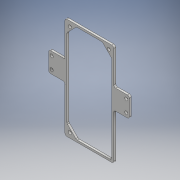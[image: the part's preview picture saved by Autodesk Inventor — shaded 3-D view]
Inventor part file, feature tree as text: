
AUTODESK INVENTOR PART (.ipt)
format: ipt  version: 2017 (Build 210142000, 142)  size: 189,952 bytes
history: native  units: mm
features: extrude x1, fillet x1, sketch x1
ambient origin geometry x8: Origin, YZ Plane, XZ Plane, XY Plane, X Axis, Y Axis, Z Axis, Center Point
bodies: Solid1 (feature_tree)
feature tree (3):
  extrude  "Extrusion1"  Depth=2.0mm
  fillet  "Fillet1"  Radius=1.0mm
  sketch  "Sketch1"  dims[d0=47.0mm d1=100.0mm d2=3.2mm d3=4.0mm d4=4.0mm d5=4.0mm d6=43.0mm d7=3.2mm d8=43.0mm d9=96.0mm d10=23.5mm d11=5.0mm d12=13.0mm d13=18.0mm d15=23.0mm d23=1.0mm d24=1.0mm d27=1.0mm d28=1.0mm d33=8.707863mm d34=9.5mm d35=45.0deg d36=45.0deg d37=9.5mm d38=45.0deg d39=3.2mm d42=3.2mm d43=12.0mm d44=4.0mm d45=3.0mm d46=4.0mm d47=3.2mm d49=3.2mm d50=12.0mm d51=3.0mm d52=2.0mm d53=0.0mm d54=2.0mm]
